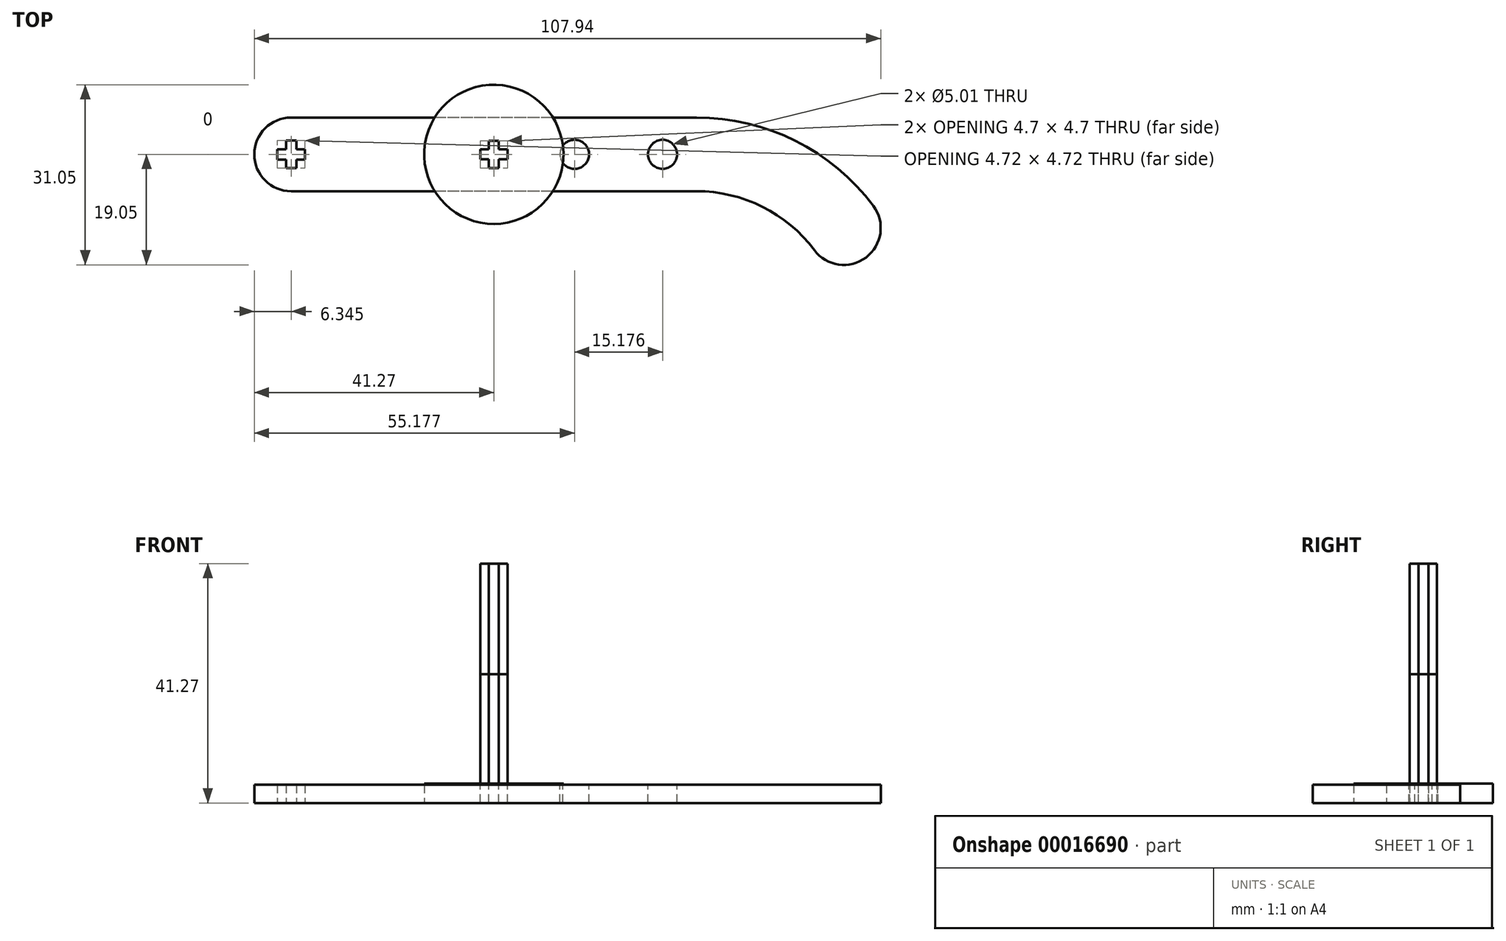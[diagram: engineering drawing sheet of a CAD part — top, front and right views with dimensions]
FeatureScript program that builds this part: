
annotation { "Feature Type Name" : "Feature", "Feature Type Description" : "" }
export const myFeature = defineFeature(function(context is Context, id is Id, definition is map)
    precondition{}
    {
        {
            var Q0;
            Q0=qCreatedBy(makeId("Top.planeOp"),FACE);
            var sketch = newSketch(context, id + "F0", { "sketchPlane" : qUnion([Q0])});
            skCircle(sketch, "E0", {"center": v(0, 0) * mm, "radius": 12 * mm});
            skSolve(sketch);
        }
        {
            var Q0;
            Q0=makeQuery(id+"F0.imprint","IMPRINT",FACE,{"disambiguationData":[TD([[makeQuery(id+"F0.imprint","IMPRINT",EDGE,{"derivedFrom":sQuery(id+"F0.wireOp",EDGE,"E0")}),1.0]])]});
            extrude(context, id + "F1", {"entities" : qUnion([Q0]), "depth" : 3.35 * mm});
        }
        {
            var Q0;
            Q0=qCreatedBy(makeId("Top.planeOp"),FACE);
            var sketch = newSketch(context, id + "F2", { "sketchPlane" : qUnion([Q0])});
            skLineSegment(sketch, "E1.rect.bottom", {"start": v(34.93, -6.35) * mm, "end": v(-34.93, -6.35) * mm});
            skLineSegment(sketch, "E1.rect.top", {"start": v(34.93, 6.35) * mm, "end": v(-34.93, 6.35) * mm});
            skLineSegment(sketch, "E1.rect.left", {"start": v(41.28, 0) * mm, "end": v(41.28, 0) * mm});
            skLineSegment(sketch, "E1.rect.right", {"start": v(-41.28, 0) * mm, "end": v(-41.28, 0) * mm});
            skPoint(sketch, "E1.rect.middle", {"position": v(0, 0) * mm});
            skPoint(sketch, "E2.visualSharp", {"position": v(-41.28, 6.35) * mm});
            skArc(sketch, "E2.filletArc", {"start": v(-34.93, 6.35) * mm, "mid": v(-39.42, 4.5) * mm, "end": v(-41.28, 0) * mm});
            skPoint(sketch, "E3.visualSharp", {"position": v(41.28, -6.35) * mm});
            skArc(sketch, "E3.filletArc", {"start": v(34.93, -6.35) * mm, "mid": v(39.42, -4.5) * mm, "end": v(41.28, 0) * mm});
            skPoint(sketch, "E4.visualSharp", {"position": v(41.28, 6.35) * mm});
            skArc(sketch, "E4.filletArc", {"start": v(41.28, 0) * mm, "mid": v(39.42, 4.5) * mm, "end": v(34.93, 6.35) * mm});
            skPoint(sketch, "E5.visualSharp", {"position": v(-41.28, -6.35) * mm});
            skArc(sketch, "E5.filletArc", {"start": v(-41.28, 0) * mm, "mid": v(-39.42, -4.5) * mm, "end": v(-34.93, -6.35) * mm});
            skCircle(sketch, "E6", {"center": v(34.93, 0) * mm, "radius": 0.8 * mm, "construction": true});
            skCircle(sketch, "E7", {"center": v(-34.93, 0) * mm, "radius": 0.8 * mm});
            skLineSegment(sketch, "E8.rect.bottom", {"start": v(-32.56, 0.89) * mm, "end": v(-37.29, 0.89) * mm});
            skLineSegment(sketch, "E8.rect.top", {"start": v(-32.56, -0.89) * mm, "end": v(-37.29, -0.89) * mm});
            skLineSegment(sketch, "E8.rect.left", {"start": v(-32.56, 0.89) * mm, "end": v(-32.56, -0.89) * mm});
            skLineSegment(sketch, "E8.rect.right", {"start": v(-37.29, 0.89) * mm, "end": v(-37.29, -0.89) * mm});
            skLineSegment(sketch, "E9.rect.bottom", {"start": v(-34.04, 2.36) * mm, "end": v(-35.81, 2.36) * mm});
            skLineSegment(sketch, "E9.rect.top", {"start": v(-34.04, -2.36) * mm, "end": v(-35.81, -2.36) * mm});
            skLineSegment(sketch, "E9.rect.left", {"start": v(-34.04, 2.36) * mm, "end": v(-34.04, -2.36) * mm});
            skLineSegment(sketch, "E9.rect.right", {"start": v(-35.81, 2.36) * mm, "end": v(-35.81, -2.36) * mm});
            skLineSegment(sketch, "E10.rect.bottom", {"start": v(37.29, 0.89) * mm, "end": v(32.56, 0.89) * mm, "construction": true});
            skLineSegment(sketch, "E10.rect.top", {"start": v(37.29, -0.89) * mm, "end": v(32.56, -0.89) * mm, "construction": true});
            skLineSegment(sketch, "E10.rect.left", {"start": v(37.29, 0.89) * mm, "end": v(37.29, -0.89) * mm, "construction": true});
            skLineSegment(sketch, "E10.rect.right", {"start": v(32.56, 0.89) * mm, "end": v(32.56, -0.89) * mm, "construction": true});
            skLineSegment(sketch, "E11.rect.bottom", {"start": v(35.81, 2.36) * mm, "end": v(34.04, 2.36) * mm, "construction": true});
            skLineSegment(sketch, "E11.rect.top", {"start": v(35.81, -2.36) * mm, "end": v(34.04, -2.36) * mm, "construction": true});
            skLineSegment(sketch, "E11.rect.left", {"start": v(35.81, 2.36) * mm, "end": v(35.81, -2.36) * mm, "construction": true});
            skLineSegment(sketch, "E11.rect.right", {"start": v(34.04, 2.36) * mm, "end": v(34.04, -2.36) * mm, "construction": true});
            skCircle(sketch, "E12", {"center": v(60.33, -12.7) * mm, "radius": 6.35 * mm});
            skArc(sketch, "E13", {"start": v(65.4, -8.89) * mm, "mid": v(51.96, 2.33) * mm, "end": v(34.93, 6.35) * mm});
            skArc(sketch, "E14", {"start": v(55.25, -16.5) * mm, "mid": v(46.28, -9.03) * mm, "end": v(34.93, -6.35) * mm});
            skSolve(sketch);
        }
        {
            var Q0;
            Q0=makeQuery(id+"F2.imprint","IMPRINT",FACE,{"disambiguationData":[TD([[makeQuery(id+"F2.imprint","IMPRINT",EDGE,{"derivedFrom":sQuery(id+"F2.wireOp",EDGE,"E1.rect.bottom")}),-1.0]])]});
            var Q1;
            {var subQ5=sQuery(id+"F2.wireOp",EDGE,"E3.filletArc");Q1=makeQuery(id+"F2.imprint","IMPRINT",FACE,{"disambiguationData":[TD([[makeQuery(id+"F2.imprint","IMPRINT",EDGE,{"derivedFrom":subQ5}),1.0]])]});}
            var Q2;
            {var subQ5=sQuery(id+"F2.wireOp",EDGE,"E2.filletArc");Q2=makeQuery(id+"F2.imprint","IMPRINT",FACE,{"disambiguationData":[TD([[makeQuery(id+"F2.imprint","IMPRINT",EDGE,{"derivedFrom":subQ5}),1.0]])]});}
            var Q3;
            Q3=makeQuery(id+"F2.imprint","IMPRINT",FACE,{"disambiguationData":[TD([[makeQuery(id+"F2.imprint","IMPRINT",EDGE,{"derivedFrom":sQuery(id+"F2.wireOp",EDGE,"E3.filletArc")}),-1.0]])]});
            var Q4;
            {var subQ0=sQuery(id+"F2.wireOp",EDGE,"E12");var subQ2=makeQuery(id+"F2.imprint","INTERSECT",VERTEX,{"derivedFrom":[subQ0,sQuery(id+"F2.wireOp",EDGE,"02e5d855-226b-4aa6-b3a8-2e928d7342dd")]});Q4=makeQuery(id+"F2.imprint","IMPRINT",FACE,{"disambiguationData":[TD([[makeQuery(id+"F2.imprint","IMPRINT",EDGE,{"disambiguationData":[TD([[subQ2,-1.0]])],"derivedFrom":subQ0}),1.0]])]});}
            extrude(context, id + "F3", {"entities" : qUnion([Q0, Q1, Q2, Q3, Q4]), "depth" : 3.17 * mm});
        }
        {
            var Q0;
            Q0=makeQuery(id+"F1.opExtrude","CAP_FACE",FACE,{"disambiguationData":[OSD([sQuery(id+"F0.wireOp",EDGE,"E0")])],"isStart":false});
            var sketch = newSketch(context, id + "F4", { "sketchPlane" : qUnion([Q0])});
            skLineSegment(sketch, "E15.rect.bottom", {"start": v(2.35, -0.88) * mm, "end": v(0.88, -0.88) * mm});
            skLineSegment(sketch, "E15.rect.top", {"start": v(2.35, 0.88) * mm, "end": v(0.88, 0.88) * mm});
            skLineSegment(sketch, "E15.rect.left", {"start": v(2.35, -0.88) * mm, "end": v(2.35, 0.88) * mm});
            skLineSegment(sketch, "E15.rect.right", {"start": v(-2.35, -0.88) * mm, "end": v(-2.35, 0.88) * mm});
            skPoint(sketch, "E15.rect.middle", {"position": v(0, 0) * mm});
            skLineSegment(sketch, "E16.rect.bottom", {"start": v(0.88, 2.35) * mm, "end": v(-0.88, 2.35) * mm});
            skLineSegment(sketch, "E16.rect.top", {"start": v(0.88, -2.35) * mm, "end": v(-0.88, -2.35) * mm});
            skLineSegment(sketch, "E16.rect.left", {"start": v(0.88, 2.35) * mm, "end": v(0.88, 0.88) * mm});
            skLineSegment(sketch, "E16.rect.right", {"start": v(-0.88, 2.35) * mm, "end": v(-0.88, 0.88) * mm});
            skLineSegment(sketch, "E17.trimOffspring", {"start": v(-0.88, 0.88) * mm, "end": v(-2.35, 0.88) * mm});
            skLineSegment(sketch, "E18.trimOffspring", {"start": v(0.88, -0.88) * mm, "end": v(0.88, -2.35) * mm});
            skLineSegment(sketch, "E19.trimOffspring", {"start": v(-0.88, -0.88) * mm, "end": v(-2.35, -0.88) * mm});
            skLineSegment(sketch, "E20.trimOffspring", {"start": v(-0.88, -0.88) * mm, "end": v(-0.88, -2.35) * mm});
            skSolve(sketch);
        }
        {
            var Q0;
            Q0=makeQuery(id+"F4.imprint","IMPRINT",FACE,{"disambiguationData":[TD([[makeQuery(id+"F4.imprint","IMPRINT",EDGE,{"derivedFrom":sQuery(id+"F4.wireOp",EDGE,"E15.rect.bottom")}),-1.0]])]});
            extrude(context, id + "F5", {"entities" : qUnion([Q0]), "operationType" : NewBodyOperationType.REMOVE, "endBound" : BoundingType.THROUGH_ALL, "oppositeDirection" : true, "depth" : 25.4 * mm});
        }
        {
            var Q0;
            Q0=makeQuery(id+"F3.opExtrude","CAP_FACE",FACE,{"disambiguationData":[OSD([sQuery(id+"F2.wireOp",EDGE,"E1.rect.bottom"),sQuery(id+"F2.wireOp",EDGE,"E1.rect.top"),sQuery(id+"F2.wireOp",EDGE,"E2.filletArc"),sQuery(id+"F2.wireOp",EDGE,"E8.rect.bottom"),sQuery(id+"F2.wireOp",EDGE,"E8.rect.top"),sQuery(id+"F2.wireOp",EDGE,"E8.rect.left"),sQuery(id+"F2.wireOp",EDGE,"E8.rect.right"),sQuery(id+"F2.wireOp",EDGE,"E9.rect.bottom"),sQuery(id+"F2.wireOp",EDGE,"E9.rect.top"),sQuery(id+"F2.wireOp",EDGE,"E9.rect.left"),sQuery(id+"F2.wireOp",EDGE,"E9.rect.right"),sQuery(id+"F2.wireOp",EDGE,"E12"),sQuery(id+"F2.wireOp",EDGE,"E13"),sQuery(id+"F2.wireOp",EDGE,"E14")])],"isStart":false});
            var sketch = newSketch(context, id + "F6", { "sketchPlane" : qUnion([Q0])});
            skLineSegment(sketch, "E21.rect.bottom", {"start": v(0.88, -2.35) * mm, "end": v(-0.88, -2.35) * mm});
            skLineSegment(sketch, "E21.rect.top", {"start": v(0.88, 2.35) * mm, "end": v(-0.88, 2.35) * mm});
            skLineSegment(sketch, "E21.rect.left", {"start": v(0.88, -2.35) * mm, "end": v(0.88, -0.88) * mm});
            skLineSegment(sketch, "E21.rect.right", {"start": v(-0.88, -2.35) * mm, "end": v(-0.88, -0.88) * mm});
            skPoint(sketch, "E21.rect.middle", {"position": v(0, 0) * mm});
            skLineSegment(sketch, "E22.rect.bottom", {"start": v(2.35, -0.88) * mm, "end": v(0.88, -0.88) * mm});
            skLineSegment(sketch, "E22.rect.top", {"start": v(2.35, 0.88) * mm, "end": v(0.88, 0.88) * mm});
            skLineSegment(sketch, "E22.rect.left", {"start": v(2.35, -0.88) * mm, "end": v(2.35, 0.88) * mm});
            skLineSegment(sketch, "E22.rect.right", {"start": v(-2.35, -0.88) * mm, "end": v(-2.35, 0.88) * mm});
            skLineSegment(sketch, "E23.trimOffspring", {"start": v(-0.88, 0.88) * mm, "end": v(-2.35, 0.88) * mm});
            skLineSegment(sketch, "E24.trimOffspring", {"start": v(0.88, 0.88) * mm, "end": v(0.88, 2.35) * mm});
            skLineSegment(sketch, "E25.trimOffspring", {"start": v(-0.88, -0.88) * mm, "end": v(-2.35, -0.88) * mm});
            skLineSegment(sketch, "E26.trimOffspring", {"start": v(-0.88, 0.88) * mm, "end": v(-0.88, 2.35) * mm});
            skSolve(sketch);
        }
        {
            var Q0;
            Q0=makeQuery(id+"F6.imprint","IMPRINT",FACE,{"disambiguationData":[TD([[makeQuery(id+"F6.imprint","IMPRINT",EDGE,{"derivedFrom":sQuery(id+"F6.wireOp",EDGE,"E21.rect.bottom")}),-1.0]])]});
            extrude(context, id + "F7", {"entities" : qUnion([Q0]), "depth" : 19.05 * mm});
        }
        {
            var Q0;
            Q0=makeQuery(id+"F3.opExtrude","CAP_FACE",FACE,{"disambiguationData":[OSD([sQuery(id+"F2.wireOp",EDGE,"E1.rect.bottom"),sQuery(id+"F2.wireOp",EDGE,"E1.rect.top"),sQuery(id+"F2.wireOp",EDGE,"E2.filletArc"),sQuery(id+"F2.wireOp",EDGE,"E8.rect.bottom"),sQuery(id+"F2.wireOp",EDGE,"E8.rect.top"),sQuery(id+"F2.wireOp",EDGE,"E8.rect.left"),sQuery(id+"F2.wireOp",EDGE,"E8.rect.right"),sQuery(id+"F2.wireOp",EDGE,"E9.rect.bottom"),sQuery(id+"F2.wireOp",EDGE,"E9.rect.top"),sQuery(id+"F2.wireOp",EDGE,"E9.rect.left"),sQuery(id+"F2.wireOp",EDGE,"E9.rect.right"),sQuery(id+"F2.wireOp",EDGE,"E12"),sQuery(id+"F2.wireOp",EDGE,"E13"),sQuery(id+"F2.wireOp",EDGE,"E14")])],"isStart":false});
            var sketch = newSketch(context, id + "F8", { "sketchPlane" : qUnion([Q0])});
            skCircle(sketch, "E27", {"center": v(-1.27, 0) * mm, "radius": 2.5 * mm});
            skCircle(sketch, "E28", {"center": v(29.08, 0) * mm, "radius": 2.5 * mm});
            skCircle(sketch, "E29", {"center": v(13.9, 0) * mm, "radius": 2.5 * mm});
            skSolve(sketch);
        }
        {
            var Q0;
            {Q0=qUnion([makeQuery(id+"F8.imprint","IMPRINT",FACE,{"disambiguationData":[TD([[makeQuery(id+"F8.imprint","IMPRINT",EDGE,{"derivedFrom":sQuery(id+"F8.wireOp",EDGE,"E27")}),1.0]])]}),makeQuery(id+"F8.imprint","IMPRINT",FACE,{"disambiguationData":[TD([[makeQuery(id+"F8.imprint","IMPRINT",EDGE,{"derivedFrom":sQuery(id+"F8.wireOp",EDGE,"E28")}),1.0]])]}),makeQuery(id+"F8.imprint","IMPRINT",FACE,{"disambiguationData":[TD([[makeQuery(id+"F8.imprint","IMPRINT",EDGE,{"derivedFrom":sQuery(id+"F8.wireOp",EDGE,"E29")}),1.0]])]})]);}
            extrude(context, id + "F9", {"entities" : qUnion([Q0]), "operationType" : NewBodyOperationType.REMOVE, "oppositeDirection" : true, "depth" : 25.4 * mm});
        }
        {
            var Q0;
            Q0=makeQuery(id+"F6.imprint","IMPRINT",FACE,{"disambiguationData":[TD([[makeQuery(id+"F6.imprint","IMPRINT",EDGE,{"derivedFrom":sQuery(id+"F6.wireOp",EDGE,"E21.rect.bottom")}),-1.0]])]});
            extrude(context, id + "F10", {"entities" : qUnion([Q0]), "depth" : 38.1 * mm});
        }
    });
